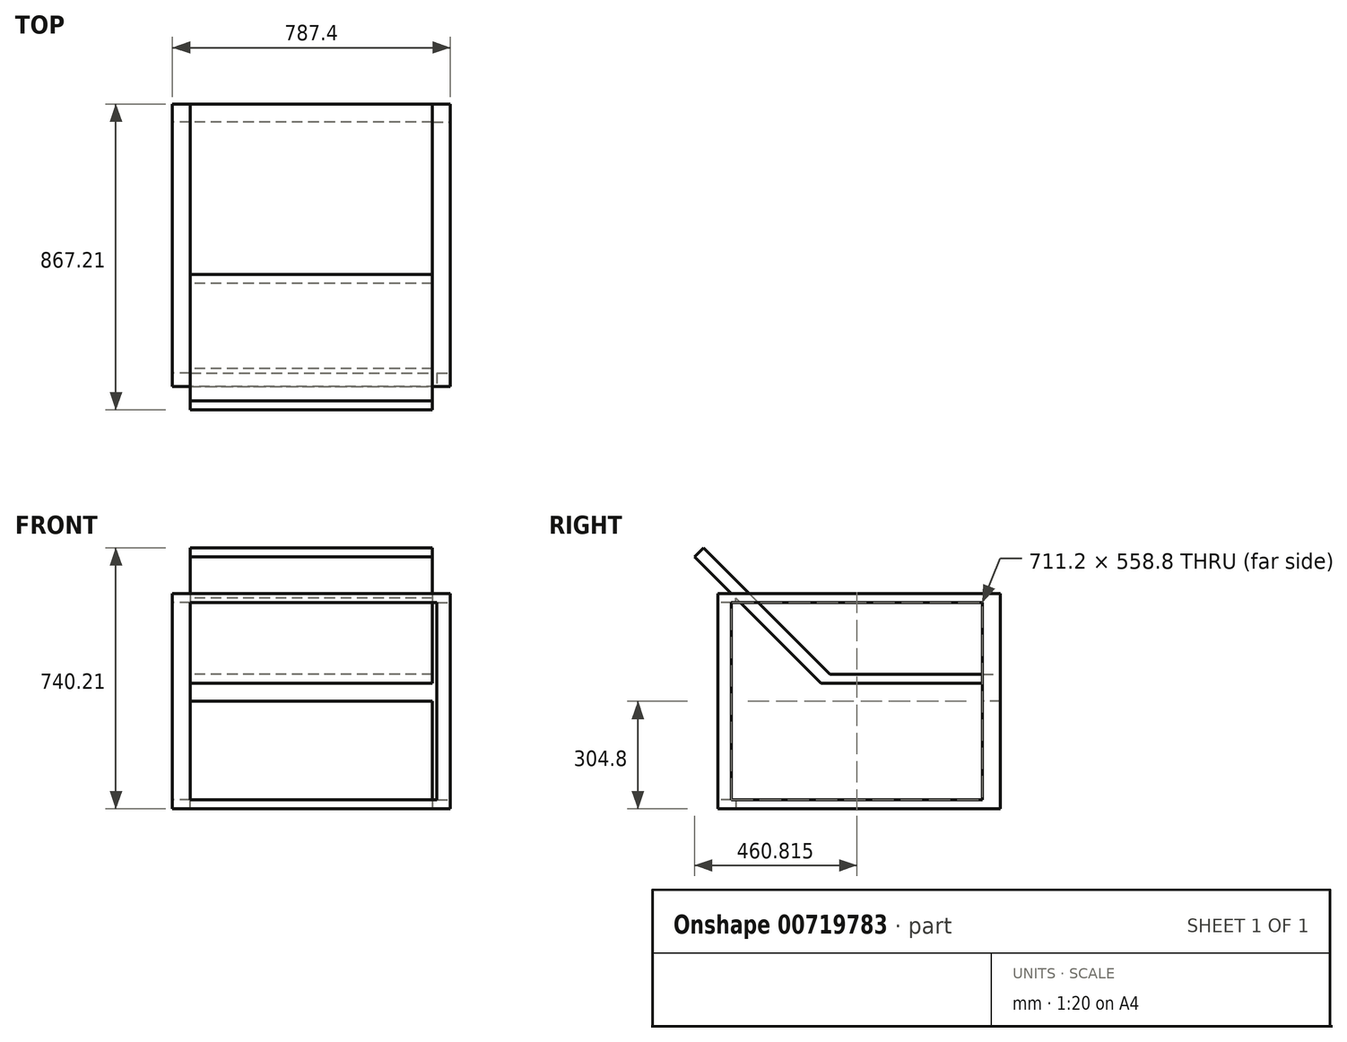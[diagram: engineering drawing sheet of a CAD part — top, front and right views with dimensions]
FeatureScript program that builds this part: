
annotation { "Feature Type Name" : "Feature", "Feature Type Description" : "" }
export const myFeature = defineFeature(function(context is Context, id is Id, definition is map)
    precondition{}
    {
        {
            var Q0;
            Q0=qCreatedBy(makeId("Top.planeOp"),FACE);
            var sketch = newSketch(context, id + "F0", { "sketchPlane" : qUnion([Q0])});
            skLineSegment(sketch, "E0.bottom", {"start": v(-119.94, -62.37) * mm, "end": v(667.46, -62.37) * mm});
            skLineSegment(sketch, "E0.top", {"start": v(-119.94, -11.57) * mm, "end": v(667.46, -11.57) * mm});
            skLineSegment(sketch, "E0.left", {"start": v(-119.94, -62.37) * mm, "end": v(-119.94, -11.57) * mm});
            skLineSegment(sketch, "E0.right", {"start": v(667.46, -62.37) * mm, "end": v(667.46, -11.57) * mm});
            skSolve(sketch);
        }
        {
            var Q0;
            Q0=makeQuery(id+"F0.imprint","IMPRINT",FACE,{"disambiguationData":[TD([[makeQuery(id+"F0.imprint","IMPRINT",EDGE,{"derivedFrom":sQuery(id+"F0.wireOp",EDGE,"E0.bottom")}),1.0]])]});
            extrude(context, id + "F1", {"entities" : qUnion([Q0]), "depth" : 609.6 * mm, "offsetDistance" : 25.4 * mm});
        }
        {
            var Q0;
            Q0=makeQuery(id+"F1.opExtrude","SWEPT_FACE",FACE,{"disambiguationData":[OSD([sQuery(id+"F0.wireOp",EDGE,"E0.bottom")])]});
            var sketch = newSketch(context, id + "F2", { "sketchPlane" : qUnion([Q0])});
            skLineSegment(sketch, "E1.bottom", {"start": v(629.36, 25.4) * mm, "end": v(-81.84, 25.4) * mm});
            skLineSegment(sketch, "E1.top", {"start": v(629.36, 584.2) * mm, "end": v(-81.84, 584.2) * mm});
            skLineSegment(sketch, "E1.left", {"start": v(629.36, 25.4) * mm, "end": v(629.36, 584.2) * mm});
            skLineSegment(sketch, "E1.right", {"start": v(-81.84, 25.4) * mm, "end": v(-81.84, 584.2) * mm});
            skPoint(sketch, "E1.middle", {"position": v(273.76, 304.8) * mm});
            skPoint(sketch, "E1.middle.positionSnap0", {"position": v(-119.94, 304.8) * mm});
            skPoint(sketch, "E1.middle.positionSnap1", {"position": v(273.76, 609.6) * mm});
            skPoint(sketch, "E1.centerSnap0", {"position": v(-119.94, 304.8) * mm});
            skPoint(sketch, "E1.centerSnap1", {"position": v(273.76, 609.6) * mm});
            skSolve(sketch);
        }
        {
            var Q0;
            Q0=makeQuery(id+"F2.imprint","IMPRINT",FACE,{"disambiguationData":[TD([[makeQuery(id+"F2.imprint","IMPRINT",EDGE,{"derivedFrom":sQuery(id+"F2.wireOp",EDGE,"E1.bottom")}),-1.0]])]});
            extrude(context, id + "F3", {"entities" : qUnion([Q0]), "operationType" : NewBodyOperationType.REMOVE, "oppositeDirection" : true, "depth" : 50.8 * mm, "offsetDistance" : 25.4 * mm});
        }
        {
            var Q0;
            Q0=makeQuery(id+"F1.opExtrude","SWEPT_FACE",FACE,{"disambiguationData":[OSD([sQuery(id+"F0.wireOp",EDGE,"E0.top")])]});
            var sketch = newSketch(context, id + "F4", { "sketchPlane" : qUnion([Q0])});
            skLineSegment(sketch, "E2.bottom", {"start": v(-667.46, 609.6) * mm, "end": v(-629.36, 609.6) * mm});
            skLineSegment(sketch, "E2.top", {"start": v(-667.46, 0) * mm, "end": v(-629.36, 0) * mm});
            skLineSegment(sketch, "E2.left", {"start": v(-667.46, 609.6) * mm, "end": v(-667.46, 0) * mm});
            skLineSegment(sketch, "E2.right", {"start": v(-629.36, 609.6) * mm, "end": v(-629.36, 0) * mm});
            skSolve(sketch);
        }
        {
            var Q0;
            Q0 = qSketchRegion(id + "F4", true);
            extrude(context, id + "F5", {"entities" : qUnion([Q0]), "operationType" : NewBodyOperationType.ADD, "depth" : 736.6 * mm, "offsetDistance" : 25.4 * mm});
        }
        {
            var Q0;
            Q0=makeQuery(id+"F5.boolean.opBoolean","MERGE",FACE,{"derivedFrom":[makeQuery(id+"F1.opExtrude","SWEPT_FACE",FACE,{"disambiguationData":[OSD([sQuery(id+"F0.wireOp",EDGE,"E0.right")])]}),makeQuery(id+"F5.opExtrude","SWEPT_FACE",FACE,{"disambiguationData":[OSD([sQuery(id+"F4.wireOp",EDGE,"E2.left")])]})]});
            var sketch = newSketch(context, id + "F6", { "sketchPlane" : qUnion([Q0])});
            skLineSegment(sketch, "E3.bottom", {"start": v(686.93, 25.4) * mm, "end": v(-24.27, 25.4) * mm});
            skLineSegment(sketch, "E3.top", {"start": v(686.93, 584.2) * mm, "end": v(-24.27, 584.2) * mm});
            skLineSegment(sketch, "E3.left", {"start": v(686.93, 25.4) * mm, "end": v(686.93, 584.2) * mm});
            skLineSegment(sketch, "E3.right", {"start": v(-24.27, 25.4) * mm, "end": v(-24.27, 584.2) * mm});
            skPoint(sketch, "E3.middle", {"position": v(331.33, 304.8) * mm});
            skPoint(sketch, "E3.middle.positionSnap0", {"position": v(725.03, 304.8) * mm});
            skPoint(sketch, "E3.middle.positionSnap1", {"position": v(331.33, 609.6) * mm});
            skPoint(sketch, "E3.centerSnap0", {"position": v(725.03, 304.8) * mm});
            skPoint(sketch, "E3.centerSnap1", {"position": v(331.33, 609.6) * mm});
            skSolve(sketch);
        }
        {
            var Q0;
            Q0=makeQuery(id+"F6.imprint","IMPRINT",FACE,{"disambiguationData":[TD([[makeQuery(id+"F6.imprint","IMPRINT",EDGE,{"derivedFrom":sQuery(id+"F6.wireOp",EDGE,"E3.bottom")}),-1.0]])]});
            extrude(context, id + "F7", {"entities" : qUnion([Q0]), "operationType" : NewBodyOperationType.REMOVE, "oppositeDirection" : true, "depth" : 50.8 * mm, "offsetDistance" : 25.4 * mm});
        }
        {
            var Q0;
            {var subQ1=sQuery(id+"F4.wireOp",EDGE,"E2.right");var subQ5=sQuery(id+"F0.wireOp",EDGE,"E0.top");Q0=makeQuery(id+"F7.boolean.opBoolean","SPLIT",FACE,{"disambiguationData":[TD([makeQuery(id+"F1.opExtrude","SWEPT_FACE",FACE,{"disambiguationData":[OSD([subQ5])]})])],"derivedFrom":makeQuery(id+"F5.boolean.opBoolean","MERGE",FACE,{"derivedFrom":[makeQuery(id+"F3.boolean.opBoolean","COPY",FACE,{"derivedFrom":makeQuery(id+"F3.opExtrude","SWEPT_FACE",FACE,{"disambiguationData":[OSD([sQuery(id+"F2.wireOp",EDGE,"E1.left")])]})}),makeQuery(id+"F5.opExtrude","SWEPT_FACE",FACE,{"disambiguationData":[OSD([subQ1])]})]})});}
            extrude(context, id + "F8", {"entities" : qUnion([Q0]), "operationType" : NewBodyOperationType.ADD, "depth" : 12.7 * mm, "offsetDistance" : 25.4 * mm});
        }
        {
            var Q0;
            Q0=makeQuery(id+"F1.opExtrude","SWEPT_FACE",FACE,{"disambiguationData":[OSD([sQuery(id+"F0.wireOp",EDGE,"E0.top")])]});
            var sketch = newSketch(context, id + "F9", { "sketchPlane" : qUnion([Q0])});
            skLineSegment(sketch, "E4.bottom", {"start": v(119.94, 609.6) * mm, "end": v(81.84, 609.6) * mm});
            skLineSegment(sketch, "E4.top", {"start": v(119.94, 0) * mm, "end": v(81.84, 0) * mm});
            skLineSegment(sketch, "E4.left", {"start": v(119.94, 609.6) * mm, "end": v(119.94, 0) * mm});
            skLineSegment(sketch, "E4.right", {"start": v(81.84, 609.6) * mm, "end": v(81.84, 0) * mm});
            skSolve(sketch);
        }
        {
            var Q0;
            {var subQ4=sQuery(id+"F9.wireOp",EDGE,"E4.bottom");Q0=makeQuery(id+"F9.imprint","IMPRINT",FACE,{"disambiguationData":[TD([[makeQuery(id+"F9.imprint","IMPRINT",EDGE,{"derivedFrom":subQ4}),1.0]])]});}
            extrude(context, id + "F10", {"entities" : qUnion([Q0]), "operationType" : NewBodyOperationType.ADD, "depth" : 736.6 * mm, "offsetDistance" : 25.4 * mm});
        }
        {
            var Q0;
            Q0=makeQuery(id+"F10.boolean.opBoolean","MERGE",FACE,{"derivedFrom":[makeQuery(id+"F3.boolean.opBoolean","COPY",FACE,{"derivedFrom":makeQuery(id+"F3.opExtrude","SWEPT_FACE",FACE,{"disambiguationData":[OSD([sQuery(id+"F2.wireOp",EDGE,"E1.right")])]})}),makeQuery(id+"F10.opExtrude","SWEPT_FACE",FACE,{"disambiguationData":[OSD([sQuery(id+"F9.wireOp",EDGE,"E4.right")])]})]});
            extrude(context, id + "F11", {"entities" : qUnion([Q0]), "operationType" : NewBodyOperationType.ADD, "depth" : 12.7 * mm, "offsetDistance" : 25.4 * mm});
        }
        {
            var Q0;
            Q0=makeQuery(id+"F10.boolean.opBoolean","MERGE",FACE,{"derivedFrom":[makeQuery(id+"F1.opExtrude","SWEPT_FACE",FACE,{"disambiguationData":[OSD([sQuery(id+"F0.wireOp",EDGE,"E0.left")])]}),makeQuery(id+"F10.opExtrude","SWEPT_FACE",FACE,{"disambiguationData":[OSD([sQuery(id+"F9.wireOp",EDGE,"E4.left")])]})]});
            var sketch = newSketch(context, id + "F12", { "sketchPlane" : qUnion([Q0])});
            skLineSegment(sketch, "E5.bottom", {"start": v(24.27, 25.4) * mm, "end": v(-686.93, 25.4) * mm});
            skLineSegment(sketch, "E5.top", {"start": v(24.27, 584.2) * mm, "end": v(-686.93, 584.2) * mm});
            skLineSegment(sketch, "E5.left", {"start": v(24.27, 25.4) * mm, "end": v(24.27, 584.2) * mm});
            skLineSegment(sketch, "E5.right", {"start": v(-686.93, 25.4) * mm, "end": v(-686.93, 584.2) * mm});
            skPoint(sketch, "E5.middle", {"position": v(-331.33, 304.8) * mm});
            skPoint(sketch, "E5.middle.positionSnap0", {"position": v(62.37, 304.8) * mm});
            skPoint(sketch, "E5.middle.positionSnap1", {"position": v(-331.33, 609.6) * mm});
            skPoint(sketch, "E5.centerSnap0", {"position": v(62.37, 304.8) * mm});
            skPoint(sketch, "E5.centerSnap1", {"position": v(-331.33, 609.6) * mm});
            skSolve(sketch);
        }
        {
            var Q0;
            Q0=makeQuery(id+"F12.imprint","IMPRINT",FACE,{"disambiguationData":[TD([[makeQuery(id+"F12.imprint","IMPRINT",EDGE,{"derivedFrom":sQuery(id+"F12.wireOp",EDGE,"E5.bottom")}),-1.0]])]});
            extrude(context, id + "F13", {"entities" : qUnion([Q0]), "operationType" : NewBodyOperationType.REMOVE, "oppositeDirection" : true, "depth" : 50.8 * mm, "offsetDistance" : 25.4 * mm});
        }
        {
            var Q0;
            {var subQ2=sQuery(id+"F0.wireOp",EDGE,"E0.top");var subQ11=sQuery(id+"F9.wireOp",EDGE,"E4.right");Q0=makeQuery(id+"F13.boolean.opBoolean","SPLIT",FACE,{"disambiguationData":[TD([makeQuery(id+"F1.opExtrude","SWEPT_FACE",FACE,{"disambiguationData":[OSD([subQ2])]})])],"derivedFrom":makeQuery(id+"F11.opExtrude","CAP_FACE",FACE,{"disambiguationData":[OSD([sQuery(id+"F2.wireOp",EDGE,"E1.right"),subQ11])],"isStart":false})});}
            var sketch = newSketch(context, id + "F14", { "sketchPlane" : qUnion([Q0])});
            skLineSegment(sketch, "E6", {"start": v(686.93, 25.4) * mm, "end": v(686.93, 304.8) * mm});
            skLineSegment(sketch, "E7.bottom", {"start": v(686.93, 304.8) * mm, "end": v(725.03, 304.8) * mm});
            skLineSegment(sketch, "E7.top", {"start": v(686.93, 355.6) * mm, "end": v(725.03, 355.6) * mm});
            skLineSegment(sketch, "E7.left", {"start": v(686.93, 304.8) * mm, "end": v(686.93, 355.6) * mm});
            skLineSegment(sketch, "E7.right", {"start": v(725.03, 304.8) * mm, "end": v(725.03, 355.6) * mm});
            skSolve(sketch);
        }
        {
            var Q0;
            Q0=makeQuery(id+"F14.imprint","IMPRINT",FACE,{"disambiguationData":[TD([[makeQuery(id+"F14.imprint","IMPRINT",EDGE,{"derivedFrom":sQuery(id+"F14.wireOp",EDGE,"E7.bottom")}),1.0]])]});
            extrude(context, id + "F15", {"entities" : qUnion([Q0]), "operationType" : NewBodyOperationType.ADD, "depth" : 711.2 * mm, "offsetDistance" : 25.4 * mm});
        }
        {
            var Q0;
            {var subQ0=sQuery(id+"F9.wireOp",EDGE,"E4.right");var subQ1=sQuery(id+"F4.wireOp",EDGE,"E2.right");Q0=makeQuery(id+"F15.boolean.opBoolean","MERGE",FACE,{"derivedFrom":[makeQuery(id+"F8.boolean.opBoolean","MERGE",FACE,{"derivedFrom":[makeQuery(id+"F5.opExtrude","CAP_FACE",FACE,{"disambiguationData":[OSD([sQuery(id+"F4.wireOp",EDGE,"E2.bottom"),sQuery(id+"F4.wireOp",EDGE,"E2.top"),sQuery(id+"F4.wireOp",EDGE,"E2.left"),subQ1])],"isStart":false}),makeQuery(id+"F8.opExtrude","SWEPT_FACE",FACE,{"disambiguationData":[OSD([subQ1]),TDD([makeQuery(id+"F5.opExtrude","CAP_EDGE",EDGE,{"disambiguationData":[OSD([subQ1])],"isStart":false})])]})]}),makeQuery(id+"F11.boolean.opBoolean","MERGE",FACE,{"derivedFrom":[makeQuery(id+"F10.opExtrude","CAP_FACE",FACE,{"disambiguationData":[OSD([sQuery(id+"F9.wireOp",EDGE,"E4.bottom"),sQuery(id+"F9.wireOp",EDGE,"E4.top"),sQuery(id+"F9.wireOp",EDGE,"E4.left"),subQ0])],"isStart":false}),makeQuery(id+"F11.opExtrude","SWEPT_FACE",FACE,{"disambiguationData":[OSD([subQ0]),TDD([makeQuery(id+"F10.opExtrude","CAP_EDGE",EDGE,{"disambiguationData":[OSD([subQ0])],"isStart":false})])]})]}),makeQuery(id+"F15.opExtrude","SWEPT_FACE",FACE,{"disambiguationData":[OSD([sQuery(id+"F14.wireOp",EDGE,"E7.right")])]})]});}
            extrude(context, id + "F16", {"entities" : qUnion([Q0]), "operationType" : NewBodyOperationType.ADD, "depth" : 12.7 * mm, "offsetDistance" : 25.4 * mm});
        }
        {
            var Q0;
            {var subQ0=sQuery(id+"F14.wireOp",EDGE,"E7.top");Q0=makeQuery(id+"F16.boolean.opBoolean","MERGE",FACE,{"derivedFrom":[makeQuery(id+"F15.opExtrude","SWEPT_FACE",FACE,{"disambiguationData":[OSD([subQ0])]}),makeQuery(id+"F16.opExtrude","SWEPT_FACE",FACE,{"disambiguationData":[OSD([sQuery(id+"F9.wireOp",EDGE,"E4.right"),subQ0,sQuery(id+"F14.wireOp",EDGE,"E7.right")])]})]});}
            var sketch = newSketch(context, id + "F17", { "sketchPlane" : qUnion([Q0])});
            skLineSegment(sketch, "E8.bottom", {"start": v(616.66, 737.73) * mm, "end": v(-69.14, 737.73) * mm});
            skLineSegment(sketch, "E8.top", {"start": v(616.66, 229.73) * mm, "end": v(-69.14, 229.73) * mm});
            skLineSegment(sketch, "E8.left", {"start": v(616.66, 737.73) * mm, "end": v(616.66, 229.73) * mm});
            skLineSegment(sketch, "E8.right", {"start": v(-69.14, 737.73) * mm, "end": v(-69.14, 229.73) * mm});
            skSolve(sketch);
        }
        {
            var Q0;
            Q0 = qSketchRegion(id + "F17", true);
            extrude(context, id + "F18", {"entities" : qUnion([Q0]), "operationType" : NewBodyOperationType.ADD, "depth" : 25.4 * mm, "offsetDistance" : 25.4 * mm});
        }
        {
            var Q0;
            Q0=makeQuery(id+"F18.opExtrude","CAP_EDGE",EDGE,{"disambiguationData":[OSD([sQuery(id+"F17.wireOp",EDGE,"E8.top")])],"isStart":false});
            chamfer(context, id + "F19", {"entities" : qUnion([Q0]), "width" : 25.4 * mm, "tangentPropagation" : true});
        }
        {
            var Q0;
            Q0=makeQuery(id+"F19.opChamfer","BLEND_FACE",FACE,{"disambiguationData":[OSD([sQuery(id+"F17.wireOp",EDGE,"E8.top")])]});
            var sketch = newSketch(context, id + "F20", { "sketchPlane" : qUnion([Q0])});
            skLineSegment(sketch, "E9.bottom", {"start": v(-69.14, 449.82) * mm, "end": v(616.66, 449.82) * mm});
            skLineSegment(sketch, "E9.top", {"start": v(-69.14, 413.9) * mm, "end": v(616.66, 413.9) * mm});
            skLineSegment(sketch, "E9.left", {"start": v(-69.14, 449.82) * mm, "end": v(-69.14, 413.9) * mm});
            skLineSegment(sketch, "E9.right", {"start": v(616.66, 449.82) * mm, "end": v(616.66, 413.9) * mm});
            skSolve(sketch);
        }
        {
            var Q0;
            Q0 = qSketchRegion(id + "F20", true);
            extrude(context, id + "F21", {"entities" : qUnion([Q0]), "operationType" : NewBodyOperationType.ADD, "depth" : 508 * mm, "offsetDistance" : 25.4 * mm});
        }
    });
